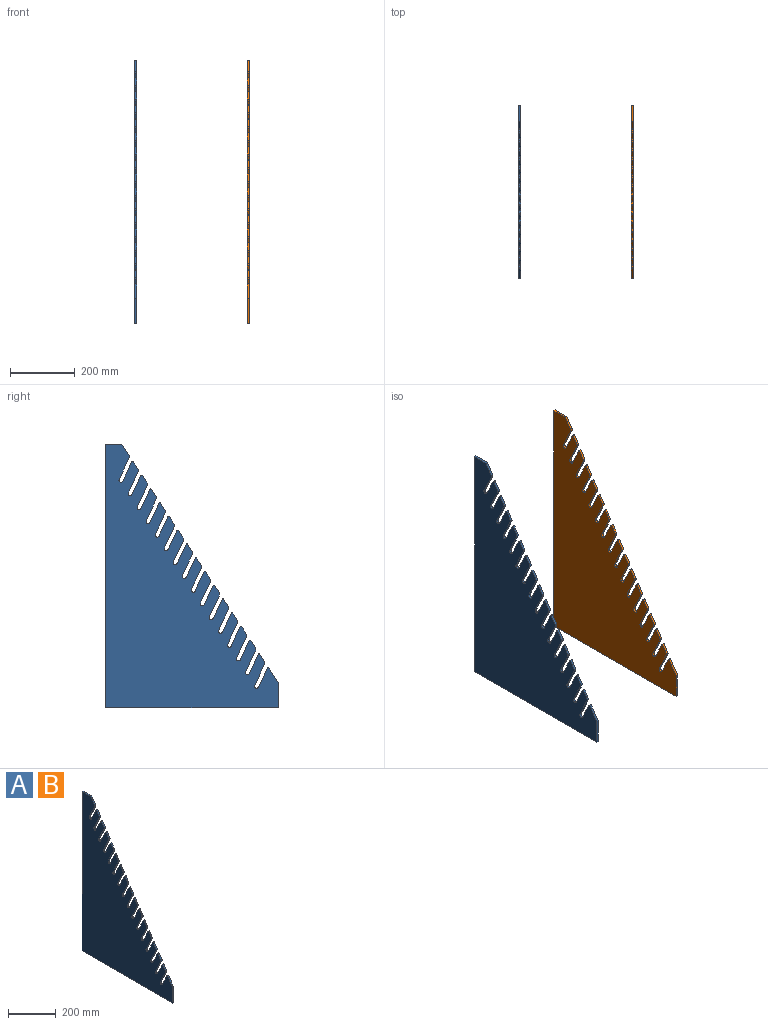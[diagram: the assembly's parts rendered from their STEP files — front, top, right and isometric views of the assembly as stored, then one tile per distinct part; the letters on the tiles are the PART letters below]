
ASSEMBLY  parts=2 mates=3
PART A: 103 faces, bbox 6.4x533.4x812.8 mm
  f0: plane 23.22x15.26mm, normal (0,-0.84,0.55), area 176.4mm2, adj f16,f17,f97,f98
  f1: plane 23.22x15.26mm, normal (0,-0.84,0.55), area 176.4mm2, adj f16,f17,f87,f88
  f2: plane 23.22x15.26mm, normal (0,-0.84,0.55), area 176.4mm2, adj f16,f17,f83,f102
  f3: plane 23.22x15.26mm, normal (0,-0.84,0.55), area 176.4mm2, adj f16,f17,f77,f78
  f4: plane 23.22x15.26mm, normal (0,-0.84,0.55), area 176.4mm2, adj f16,f17,f72,f93
  f5: plane 23.22x15.26mm, normal (0,-0.84,0.55), area 176.4mm2, adj f16,f17,f67,f68
  f6: plane 23.22x15.26mm, normal (0,-0.84,0.55), area 176.4mm2, adj f16,f17,f63,f82
  f7: plane 23.22x15.26mm, normal (0,-0.84,0.55), area 176.4mm2, adj f16,f17,f57,f58
  f8: plane 34.35x22.57mm, normal (0,-0.84,0.55), area 261mm2, adj f16,f17,f22,f52
  f9: plane 23.22x15.26mm, normal (0,-0.84,0.55), area 176.4mm2, adj f16,f17,f48,f62
  f10: plane 23.22x15.26mm, normal (0,-0.84,0.55), area 176.4mm2, adj f16,f17,f42,f43
  f11: plane 23.22x15.26mm, normal (0,-0.84,0.55), area 176.4mm2, adj f16,f17,f38,f92
  f12: plane 23.22x15.26mm, normal (0,-0.84,0.55), area 176.4mm2, adj f16,f17,f37,f53
  f13: plane 23.22x15.26mm, normal (0,-0.84,0.55), area 176.4mm2, adj f16,f17,f32,f33
  f14: plane 23.22x15.26mm, normal (0,-0.84,0.55), area 176.4mm2, adj f16,f17,f28,f47
  f15: plane 23.22x15.26mm, normal (0,-0.84,0.55), area 176.4mm2, adj f16,f17,f27,f73
  f16: plane 812.8x533.4mm, normal (1,0,0), area 239695mm2, adj f0,f1,f2,f3,f4,f5,f6,f7
  f17: plane 812.8x533.4mm, normal (-1,0,0), area 239695mm2, adj f0,f1,f2,f3,f4,f5,f6,f7
  f18: plane 812.8x6.35mm, normal (0,1,0), area 5161.3mm2, adj f16,f17,f20,f22
  f19: plane 45.1x29.64mm, normal (0,-0.84,0.55), area 342.7mm2, adj f16,f17,f21,f23
  f20: plane 533.4x6.35mm, normal (0,0,-1), area 3387.1mm2, adj f16,f17,f18,f21
  f21: plane 77.3x6.35mm, normal (0,-1,0), area 490.9mm2, adj f16,f17,f19,f20
  f22: plane 50.07x6.35mm, normal (0,0,1), area 318mm2, adj f8,f16,f17,f18
  f23: cylinder r=2.54mm len=6.35mm, axis (1,0,0), area 34.3mm2, adj f16,f17,f19,f24
  f24: plane 59.18x27.6mm, normal (0,0.91,0.42), area 414.6mm2, adj f16,f17,f23,f25
  f25: cylinder r=6.35mm len=12.11mm, axis (1,0,0), area 126.7mm2, adj f16,f17,f24,f26
  f26: plane 67.2x31.34mm, normal (0,-0.91,-0.42), area 470.8mm2, adj f16,f17,f25,f27
  f27: cylinder r=6.35mm len=6.35mm, axis (1,0,0), area 41mm2, adj f15,f16,f17,f26
  f28: cylinder r=2.54mm len=6.35mm, axis (1,0,0), area 34.3mm2, adj f14,f16,f17,f29
  f29: plane 59.18x27.6mm, normal (0,0.91,0.42), area 414.6mm2, adj f16,f17,f28,f30
  f30: cylinder r=6.35mm len=12.11mm, axis (1,0,0), area 126.7mm2, adj f16,f17,f29,f31
  f31: plane 67.2x31.34mm, normal (0,-0.91,-0.42), area 470.8mm2, adj f16,f17,f30,f32
  f32: cylinder r=6.35mm len=6.35mm, axis (1,0,0), area 41mm2, adj f13,f16,f17,f31
  f33: cylinder r=2.54mm len=6.35mm, axis (1,0,0), area 34.3mm2, adj f13,f16,f17,f34
  f34: plane 59.18x27.6mm, normal (0,0.91,0.42), area 414.6mm2, adj f16,f17,f33,f35
  f35: cylinder r=6.35mm len=12.11mm, axis (1,0,0), area 126.7mm2, adj f16,f17,f34,f36
  f36: plane 67.2x31.34mm, normal (0,-0.91,-0.42), area 470.8mm2, adj f16,f17,f35,f37
  f37: cylinder r=6.35mm len=6.35mm, axis (1,0,0), area 41mm2, adj f12,f16,f17,f36
  f38: cylinder r=2.54mm len=6.35mm, axis (1,0,0), area 34.3mm2, adj f11,f16,f17,f39
  f39: plane 59.18x27.6mm, normal (0,0.91,0.42), area 414.6mm2, adj f16,f17,f38,f40
  f40: cylinder r=6.35mm len=12.11mm, axis (1,0,0), area 126.7mm2, adj f16,f17,f39,f41
  f41: plane 67.2x31.34mm, normal (0,-0.91,-0.42), area 470.8mm2, adj f16,f17,f40,f42
  f42: cylinder r=6.35mm len=6.35mm, axis (1,0,0), area 41mm2, adj f10,f16,f17,f41
  f43: cylinder r=2.54mm len=6.35mm, axis (1,0,0), area 34.3mm2, adj f10,f16,f17,f44
  f44: plane 59.18x27.6mm, normal (0,0.91,0.42), area 414.6mm2, adj f16,f17,f43,f45
  f45: cylinder r=6.35mm len=12.11mm, axis (1,0,0), area 126.7mm2, adj f16,f17,f44,f46
  f46: plane 67.2x31.34mm, normal (0,-0.91,-0.42), area 470.8mm2, adj f16,f17,f45,f47
  f47: cylinder r=6.35mm len=6.35mm, axis (1,0,0), area 41mm2, adj f14,f16,f17,f46
  f48: cylinder r=2.54mm len=6.35mm, axis (1,0,0), area 34.3mm2, adj f9,f16,f17,f49
  f49: plane 59.18x27.6mm, normal (0,0.91,0.42), area 414.6mm2, adj f16,f17,f48,f50
  f50: cylinder r=6.35mm len=12.11mm, axis (1,0,0), area 126.7mm2, adj f16,f17,f49,f51
  f51: plane 67.2x31.34mm, normal (0,-0.91,-0.42), area 470.8mm2, adj f16,f17,f50,f52
  f52: cylinder r=6.35mm len=6.35mm, axis (1,0,0), area 41mm2, adj f8,f16,f17,f51
  f53: cylinder r=2.54mm len=6.35mm, axis (1,0,0), area 34.3mm2, adj f12,f16,f17,f54
  f54: plane 59.18x27.6mm, normal (0,0.91,0.42), area 414.6mm2, adj f16,f17,f53,f55
  f55: cylinder r=6.35mm len=12.11mm, axis (1,0,0), area 126.7mm2, adj f16,f17,f54,f56
  f56: plane 67.2x31.34mm, normal (0,-0.91,-0.42), area 470.8mm2, adj f16,f17,f55,f57
  f57: cylinder r=6.35mm len=6.35mm, axis (1,0,0), area 41mm2, adj f7,f16,f17,f56
  f58: cylinder r=2.54mm len=6.35mm, axis (1,0,0), area 34.3mm2, adj f7,f16,f17,f59
  f59: plane 59.18x27.6mm, normal (0,0.91,0.42), area 414.6mm2, adj f16,f17,f58,f60
  f60: cylinder r=6.35mm len=12.11mm, axis (1,0,0), area 126.7mm2, adj f16,f17,f59,f61
  f61: plane 67.2x31.34mm, normal (0,-0.91,-0.42), area 470.8mm2, adj f16,f17,f60,f62
  f62: cylinder r=6.35mm len=6.35mm, axis (1,0,0), area 41mm2, adj f9,f16,f17,f61
  f63: cylinder r=2.54mm len=6.35mm, axis (1,0,0), area 34.3mm2, adj f6,f16,f17,f64
  f64: plane 59.18x27.6mm, normal (0,0.91,0.42), area 414.6mm2, adj f16,f17,f63,f65
  f65: cylinder r=6.35mm len=12.11mm, axis (1,0,0), area 126.7mm2, adj f16,f17,f64,f66
  f66: plane 67.2x31.34mm, normal (0,-0.91,-0.42), area 470.8mm2, adj f16,f17,f65,f67
  f67: cylinder r=6.35mm len=6.35mm, axis (1,0,0), area 41mm2, adj f5,f16,f17,f66
  f68: cylinder r=2.54mm len=6.35mm, axis (1,0,0), area 34.3mm2, adj f5,f16,f17,f69
  f69: plane 59.18x27.6mm, normal (0,0.91,0.42), area 414.6mm2, adj f16,f17,f68,f70
  f70: cylinder r=6.35mm len=12.11mm, axis (1,0,0), area 126.7mm2, adj f16,f17,f69,f71
  f71: plane 67.2x31.34mm, normal (0,-0.91,-0.42), area 470.8mm2, adj f16,f17,f70,f72
  f72: cylinder r=6.35mm len=6.35mm, axis (1,0,0), area 41mm2, adj f4,f16,f17,f71
  f73: cylinder r=2.54mm len=6.35mm, axis (1,0,0), area 34.3mm2, adj f15,f16,f17,f74
  f74: plane 59.18x27.6mm, normal (0,0.91,0.42), area 414.6mm2, adj f16,f17,f73,f75
  f75: cylinder r=6.35mm len=12.11mm, axis (1,0,0), area 126.7mm2, adj f16,f17,f74,f76
  f76: plane 67.2x31.34mm, normal (0,-0.91,-0.42), area 470.8mm2, adj f16,f17,f75,f77
  f77: cylinder r=6.35mm len=6.35mm, axis (1,0,0), area 41mm2, adj f3,f16,f17,f76
  f78: cylinder r=2.54mm len=6.35mm, axis (1,0,0), area 34.3mm2, adj f3,f16,f17,f79
  f79: plane 59.18x27.6mm, normal (0,0.91,0.42), area 414.6mm2, adj f16,f17,f78,f80
  f80: cylinder r=6.35mm len=12.11mm, axis (1,0,0), area 126.7mm2, adj f16,f17,f79,f81
  f81: plane 67.2x31.34mm, normal (0,-0.91,-0.42), area 470.8mm2, adj f16,f17,f80,f82
  f82: cylinder r=6.35mm len=6.35mm, axis (1,0,0), area 41mm2, adj f6,f16,f17,f81
  f83: cylinder r=2.54mm len=6.35mm, axis (1,0,0), area 34.3mm2, adj f2,f16,f17,f84
  f84: plane 59.18x27.6mm, normal (0,0.91,0.42), area 414.6mm2, adj f16,f17,f83,f85
  f85: cylinder r=6.35mm len=12.11mm, axis (1,0,0), area 126.7mm2, adj f16,f17,f84,f86
  f86: plane 67.2x31.34mm, normal (0,-0.91,-0.42), area 470.8mm2, adj f16,f17,f85,f87
  f87: cylinder r=6.35mm len=6.35mm, axis (1,0,0), area 41mm2, adj f1,f16,f17,f86
  f88: cylinder r=2.54mm len=6.35mm, axis (1,0,0), area 34.3mm2, adj f1,f16,f17,f89
  f89: plane 59.18x27.6mm, normal (0,0.91,0.42), area 414.6mm2, adj f16,f17,f88,f90
  f90: cylinder r=6.35mm len=12.11mm, axis (1,0,0), area 126.7mm2, adj f16,f17,f89,f91
  f91: plane 67.2x31.34mm, normal (0,-0.91,-0.42), area 470.8mm2, adj f16,f17,f90,f92
  f92: cylinder r=6.35mm len=6.35mm, axis (1,0,0), area 41mm2, adj f11,f16,f17,f91
  f93: cylinder r=2.54mm len=6.35mm, axis (1,0,0), area 34.3mm2, adj f4,f16,f17,f94
  f94: plane 59.18x27.6mm, normal (0,0.91,0.42), area 414.6mm2, adj f16,f17,f93,f95
  f95: cylinder r=6.35mm len=12.11mm, axis (1,0,0), area 126.7mm2, adj f16,f17,f94,f96
  f96: plane 67.2x31.34mm, normal (0,-0.91,-0.42), area 470.8mm2, adj f16,f17,f95,f97
  f97: cylinder r=6.35mm len=6.35mm, axis (1,0,0), area 41mm2, adj f0,f16,f17,f96
  f98: cylinder r=2.54mm len=6.35mm, axis (1,0,0), area 34.3mm2, adj f0,f16,f17,f99
  f99: plane 59.18x27.6mm, normal (0,0.91,0.42), area 414.6mm2, adj f16,f17,f98,f100
  f100: cylinder r=6.35mm len=12.11mm, axis (1,0,0), area 126.7mm2, adj f16,f17,f99,f101
  f101: plane 67.2x31.34mm, normal (0,-0.91,-0.42), area 470.8mm2, adj f16,f17,f100,f102
  f102: cylinder r=6.35mm len=6.35mm, axis (1,0,0), area 41mm2, adj f2,f16,f17,f101
PART B: same geometry as A
PLACE A at identity fixed
PLACE B t=(346.61,0,0)mm
MATE planar A.f22 <-> B.f22  axis (0,0,1) through (6.35,-25.04,812.8)mm
MATE planar A.f18 <-> B.f18  axis (0,1,0) through (6.35,0,406.4)mm
MATE parallel B.f17 <-> A.f17  axis (-1,0,0) through (346.61,-188.09,286.23)mm
